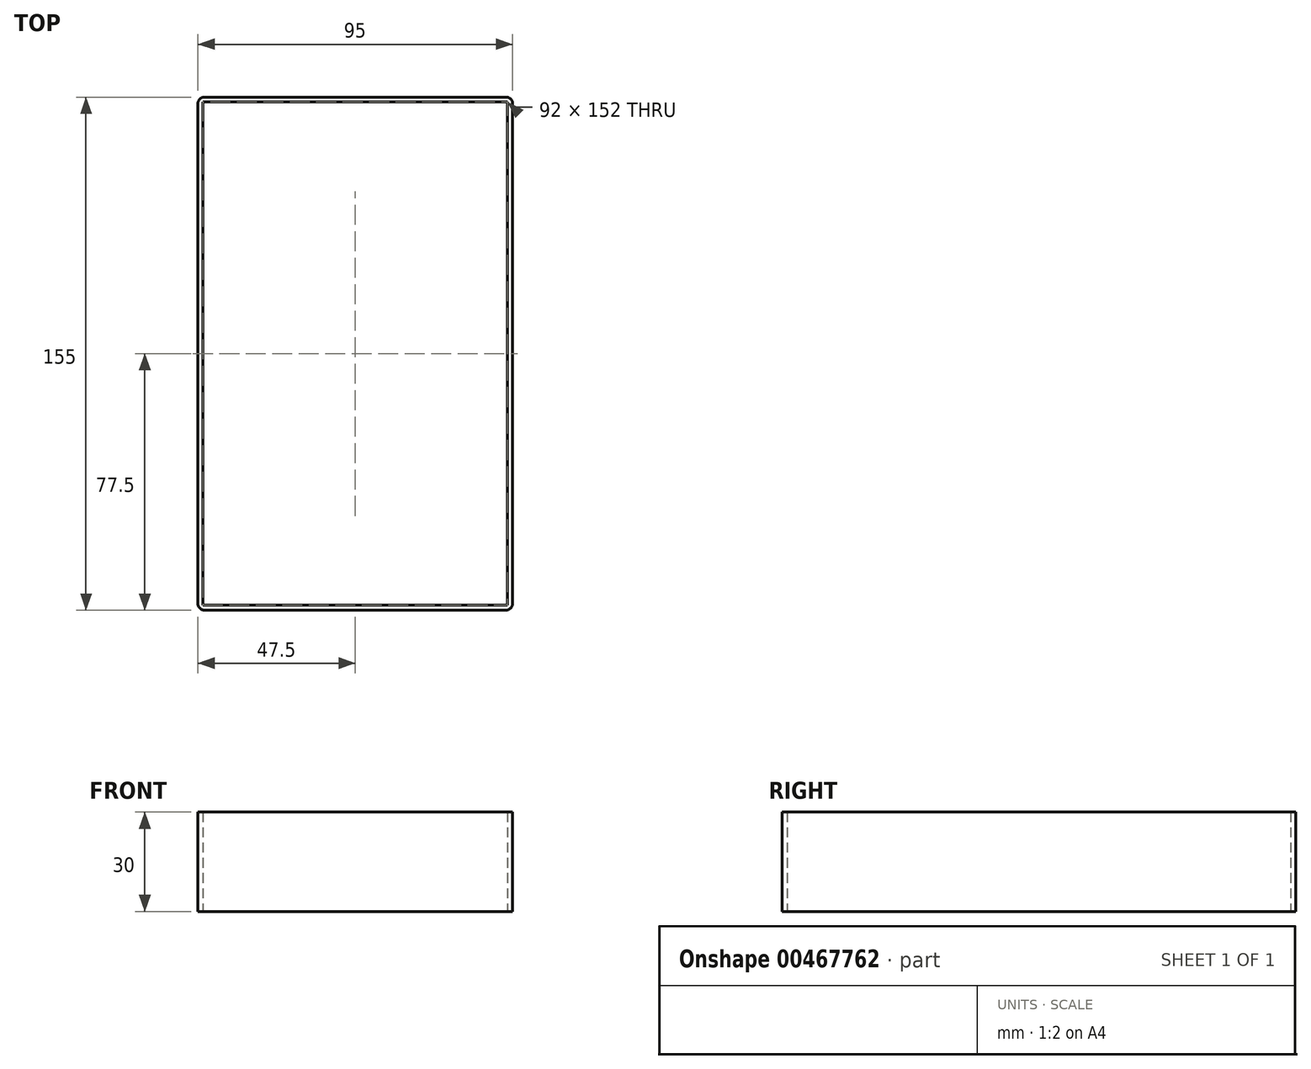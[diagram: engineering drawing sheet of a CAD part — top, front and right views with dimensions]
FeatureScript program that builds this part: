
annotation { "Feature Type Name" : "Feature", "Feature Type Description" : "" }
export const myFeature = defineFeature(function(context is Context, id is Id, definition is map)
    precondition{}
    {
        {
            var Q0;
            Q0=qCreatedBy(makeId("Top.planeOp"),FACE);
            var sketch = newSketch(context, id + "F0", { "sketchPlane" : qUnion([Q0])});
            skLineSegment(sketch, "E0.bottom", {"start": v(46, -76) * mm, "end": v(-46, -76) * mm});
            skLineSegment(sketch, "E0.top", {"start": v(46, 76) * mm, "end": v(-46, 76) * mm});
            skLineSegment(sketch, "E0.left", {"start": v(46, -76) * mm, "end": v(46, 76) * mm});
            skLineSegment(sketch, "E0.right", {"start": v(-46, -76) * mm, "end": v(-46, 76) * mm});
            skPoint(sketch, "E0.middle", {"position": v(0, 0) * mm});
            skSolve(sketch);
        }
        {
            var Q0;
            Q0=makeQuery(id+"F0.imprint","IMPRINT",FACE,{"disambiguationData":[TD([[makeQuery(id+"F0.imprint","IMPRINT",EDGE,{"derivedFrom":sQuery(id+"F0.wireOp",EDGE,"E0.bottom")}),-1.0]])]});
            var sketch = newSketch(context, id + "F1", { "sketchPlane" : qUnion([Q0])});
            skLineSegment(sketch, "E1.0", {"start": v(47.5, -77.5) * mm, "end": v(47.5, 77.5) * mm});
            skLineSegment(sketch, "E1.1", {"start": v(-47.5, -77.5) * mm, "end": v(47.5, -77.5) * mm});
            skLineSegment(sketch, "E1.2", {"start": v(-47.5, 77.5) * mm, "end": v(-47.5, -77.5) * mm});
            skLineSegment(sketch, "E1.3", {"start": v(47.5, 77.5) * mm, "end": v(-47.5, 77.5) * mm});
            skSolve(sketch);
        }
        {
            var Q0;
            Q0=makeQuery(id+"F1.imprint","IMPRINT",FACE,{"disambiguationData":[TD([[makeQuery(id+"F1.imprint","IMPRINT",EDGE,{"derivedFrom":sQuery(id+"F1.wireOp",EDGE,"E1.0")}),1.0]])]});
            extrude(context, id + "F2", {"entities" : qUnion([Q0]), "depth" : 30 * mm});
        }
        {
            var Q0;
            Q0=makeQuery(id+"F2.opExtrude","SWEPT_EDGE",EDGE,{"disambiguationData":[OSD([sQuery(id+"F1.wireOp",EDGE,"E1.0"),sQuery(id+"F1.wireOp",EDGE,"E1.3")])]});
            var Q1;
            Q1=makeQuery(id+"F2.opExtrude","SWEPT_EDGE",EDGE,{"disambiguationData":[OSD([sQuery(id+"F1.wireOp",EDGE,"E1.2"),sQuery(id+"F1.wireOp",EDGE,"E1.3")])]});
            var Q2;
            Q2=makeQuery(id+"F2.opExtrude","SWEPT_EDGE",EDGE,{"disambiguationData":[OSD([sQuery(id+"F1.wireOp",EDGE,"E1.1"),sQuery(id+"F1.wireOp",EDGE,"E1.2")])]});
            var Q3;
            Q3=makeQuery(id+"F2.opExtrude","SWEPT_EDGE",EDGE,{"disambiguationData":[OSD([sQuery(id+"F1.wireOp",EDGE,"E1.0"),sQuery(id+"F1.wireOp",EDGE,"E1.1")])]});
            fillet(context, id + "F3", {"entities" : qUnion([Q0, Q1, Q2, Q3]), "radius" : 2 * mm, "tangentPropagation" : true, "allowEdgeOverflow" : false});
        }
    });
